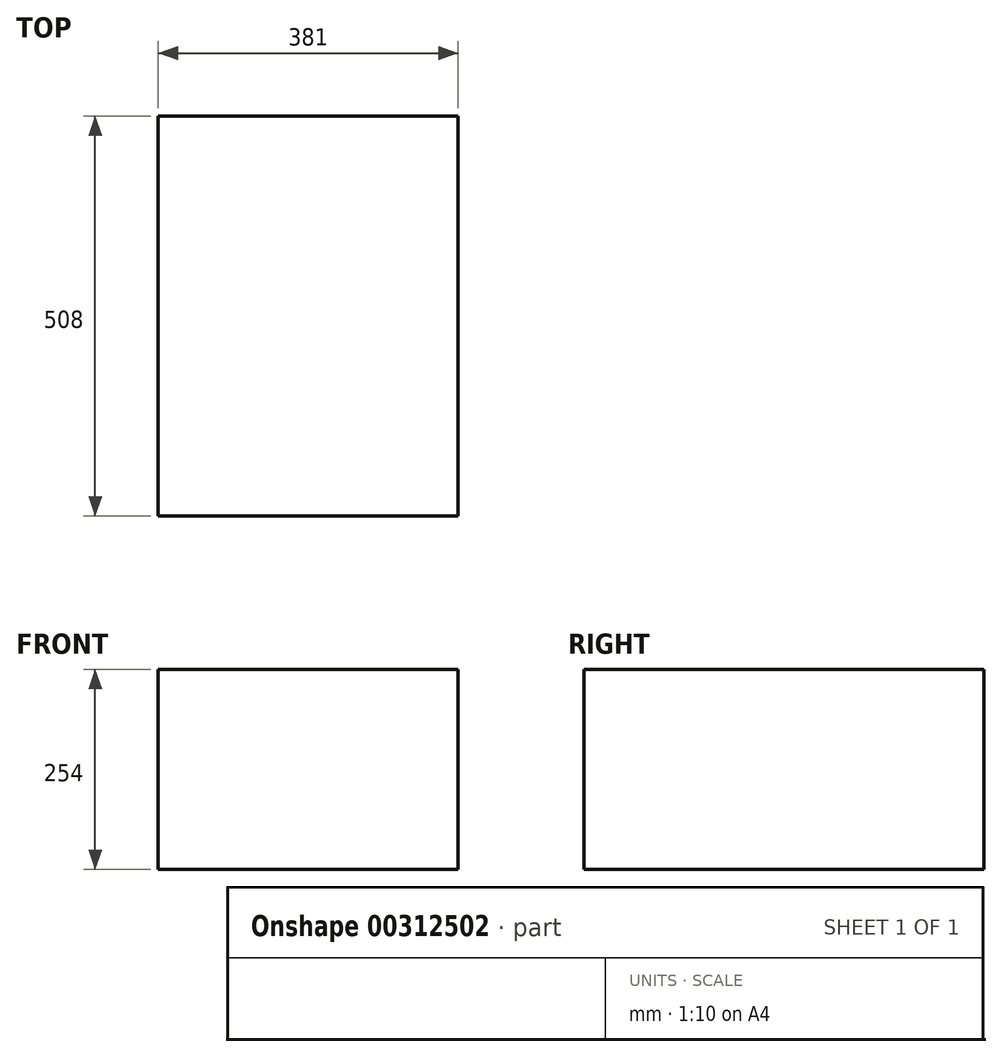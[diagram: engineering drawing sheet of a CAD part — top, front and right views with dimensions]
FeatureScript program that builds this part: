
annotation { "Feature Type Name" : "Feature", "Feature Type Description" : "" }
export const myFeature = defineFeature(function(context is Context, id is Id, definition is map)
    precondition{}
    {
        {
            var Q0;
            Q0=qCreatedBy(makeId("Top.planeOp"),FACE);
            var sketch = newSketch(context, id + "F0", { "sketchPlane" : qUnion([Q0])});
            skLineSegment(sketch, "E0.bottom", {"start": v(0, 0) * mm, "end": v(-381, 0) * mm});
            skLineSegment(sketch, "E0.top", {"start": v(0, -508) * mm, "end": v(-381, -508) * mm});
            skLineSegment(sketch, "E0.left", {"start": v(0, 0) * mm, "end": v(0, -508) * mm});
            skLineSegment(sketch, "E0.right", {"start": v(-381, 0) * mm, "end": v(-381, -508) * mm});
            skSolve(sketch);
        }
        {
            var Q0;
            Q0 = qSketchRegion(id + "F0", true);
            extrude(context, id + "F1", {"entities" : qUnion([Q0]), "oppositeDirection" : true, "depth" : 254 * mm});
        }
    });
